# Revit family: Sink_Undermount_Stainless_Steel-Elkay-ELUHAD191655PD
name_source: partatom
category: Plumbing Fixtures
units: mm (PartAtom-declared; Revit-internal decimal feet)

## family parameters
Cut with Voids When Loaded = No
Host = Face
Maintain Annotation Orientation = No
OmniClass Number = 23.45.05.14.14
OmniClass Title = Sinks/Lavatories
Part Type = Normal
Room Calculation Point = No
Round Connector Dimension = Use Diameter
Shared = No

## types (1)
- ELUHAD191655PD (Single Bowl Undermount Sink)
    Approx. Shipping Weight (lbs) = 17
    Assembly Code = D2010410
    Bowl 1 Dimensions = 19  inch x 16 inch x 5 3/8 inch
    Default Elevation = 48 "
    Description = Lustertone Classic Stainless Steel 21 1/2 inch x 18 1/2 inch x 5 3/8 inch Single Bowl Undermount ADA Sink w/Perfect Drain®
    Drain Location = Rear Center
    Drain Size = 3.375
    Gauge = 18
    Installation type = Undermount
    Main Material = Finish-Elkay-Stainless Steel
    Manufacturer = Elkay Manufacturer Company
    Manufacturer Brand = Elkay(Elkay (by Zurn Elkay Water Solutions)
    Model = ELUHAD191655PD
    Number of Bowls = 1
    Outlet Connection Size (inch) = 1.5 "
    Product Documentation Link = https://www.elkayfiles.com
    Product Installation Sheet URL = https://www.elkayfiles.com
    Product Page URL = https://www.elkay.com
    Product Weight (lbs) = 15
    Product data URL = https://www.bimobject.com
    Radius = 1.75 "
    Radius 2 = 2.25 "
    Repair Parts URL = https://www.elkayfiles.com
    Sink Dimensions = 21 1/2 inch x 18 1/2 inch x 5 3/8 inch
    URL = https://www.elkay.com
    Undermount sink = 1 "
    Waste Connection = Yes

## geometry (parser evidence)
native form markers: Sweep x6
no freeform markers — native parametric forms only
